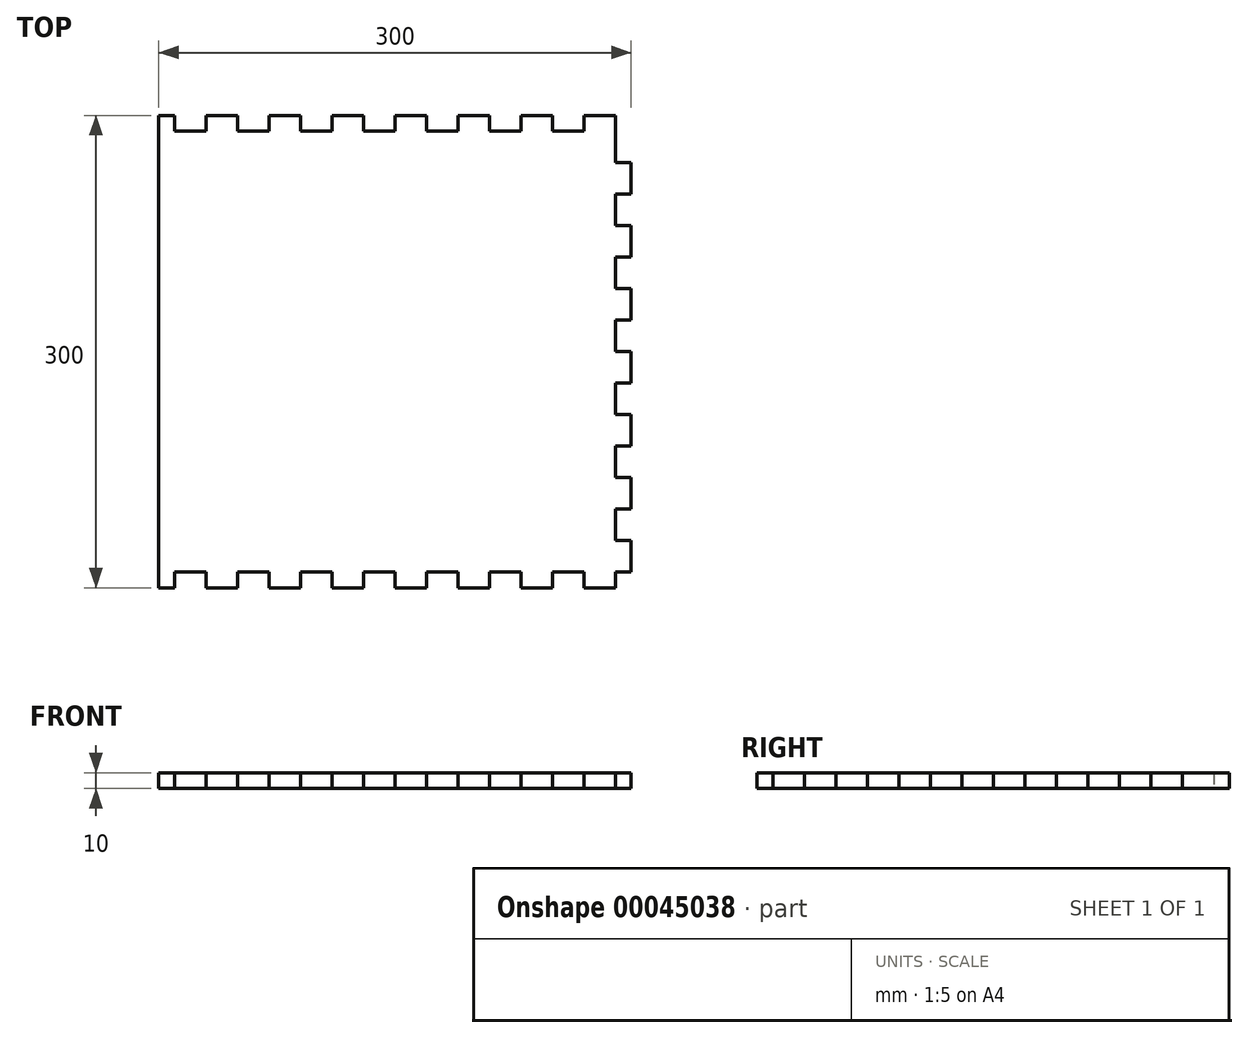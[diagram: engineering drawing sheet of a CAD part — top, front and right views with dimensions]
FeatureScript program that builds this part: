
annotation { "Feature Type Name" : "Feature", "Feature Type Description" : "" }
export const myFeature = defineFeature(function(context is Context, id is Id, definition is map)
    precondition{}
    {
        {
            var Q0;
            Q0=qCreatedBy(makeId("Top.planeOp"),FACE);
            var sketch = newSketch(context, id + "F0", { "sketchPlane" : qUnion([Q0])});
            skLineSegment(sketch, "E0.bottom", {"start": v(0, 0) * mm, "end": v(300, 0) * mm});
            skLineSegment(sketch, "E0.top", {"start": v(0, 300) * mm, "end": v(300, 300) * mm});
            skLineSegment(sketch, "E0.left", {"start": v(0, 0) * mm, "end": v(0, 300) * mm});
            skLineSegment(sketch, "E0.right", {"start": v(300, 0) * mm, "end": v(300, 300) * mm});
            skSolve(sketch);
        }
        {
            var Q0;
            Q0 = qSketchRegion(id + "F0", true);
            extrude(context, id + "F1", {"entities" : qUnion([Q0]), "depth" : 10 * mm});
        }
        {
            var Q0;
            Q0=makeQuery(id+"F0.imprint","IMPRINT",FACE,{"disambiguationData":[TD([[makeQuery(id+"F0.imprint","IMPRINT",EDGE,{"derivedFrom":sQuery(id+"F0.wireOp",EDGE,"E0.bottom")}),1.0]])]});
            var sketch = newSketch(context, id + "F2", { "sketchPlane" : qUnion([Q0])});
            skLineSegment(sketch, "E1.bottom", {"start": v(10, 0) * mm, "end": v(29.92, 0) * mm});
            skLineSegment(sketch, "E1.top", {"start": v(10, 10) * mm, "end": v(29.93, 10) * mm});
            skLineSegment(sketch, "E1.left", {"start": v(10, 0) * mm, "end": v(10, 10) * mm});
            skLineSegment(sketch, "E1.right", {"start": v(29.93, 0) * mm, "end": v(29.93, 10) * mm});
            skLineSegment(sketch, "E2.1.0.0", {"start": v(50, 0) * mm, "end": v(50, 10) * mm});
            skLineSegment(sketch, "E2.1.0.1", {"start": v(50, 0) * mm, "end": v(69.92, 0) * mm});
            skLineSegment(sketch, "E2.1.0.2", {"start": v(69.92, 0) * mm, "end": v(69.92, 10) * mm});
            skLineSegment(sketch, "E2.1.0.3", {"start": v(50, 10) * mm, "end": v(69.92, 10) * mm});
            skLineSegment(sketch, "E2.2.0.0", {"start": v(90, 0) * mm, "end": v(90, 10) * mm});
            skLineSegment(sketch, "E2.2.0.1", {"start": v(90, 0) * mm, "end": v(109.92, 0) * mm});
            skLineSegment(sketch, "E2.2.0.2", {"start": v(109.93, 0) * mm, "end": v(109.93, 10) * mm});
            skLineSegment(sketch, "E2.2.0.3", {"start": v(90, 10) * mm, "end": v(109.93, 10) * mm});
            skLineSegment(sketch, "E2.3.0.0", {"start": v(130, 0) * mm, "end": v(130, 10) * mm});
            skLineSegment(sketch, "E2.3.0.1", {"start": v(130, 0) * mm, "end": v(149.93, 0) * mm});
            skLineSegment(sketch, "E2.3.0.2", {"start": v(149.93, 0) * mm, "end": v(149.93, 10) * mm});
            skLineSegment(sketch, "E2.3.0.3", {"start": v(130, 10) * mm, "end": v(149.93, 10) * mm});
            skLineSegment(sketch, "E2.4.0.0", {"start": v(170, 0) * mm, "end": v(170, 10) * mm});
            skLineSegment(sketch, "E2.4.0.1", {"start": v(170, 0) * mm, "end": v(189.92, 0) * mm});
            skLineSegment(sketch, "E2.4.0.2", {"start": v(189.93, 0) * mm, "end": v(189.93, 10) * mm});
            skLineSegment(sketch, "E2.4.0.3", {"start": v(170, 10) * mm, "end": v(189.92, 10) * mm});
            skLineSegment(sketch, "E2.5.0.0", {"start": v(210, 0) * mm, "end": v(210, 10) * mm});
            skLineSegment(sketch, "E2.5.0.1", {"start": v(210, 0) * mm, "end": v(229.93, 0) * mm});
            skLineSegment(sketch, "E2.5.0.2", {"start": v(229.93, 0) * mm, "end": v(229.93, 10) * mm});
            skLineSegment(sketch, "E2.5.0.3", {"start": v(210, 10) * mm, "end": v(229.93, 10) * mm});
            skLineSegment(sketch, "E2.6.0.0", {"start": v(250, 0) * mm, "end": v(250, 10) * mm});
            skLineSegment(sketch, "E2.6.0.1", {"start": v(250, 0) * mm, "end": v(269.93, 0) * mm});
            skLineSegment(sketch, "E2.6.0.2", {"start": v(269.92, 0) * mm, "end": v(269.92, 10) * mm});
            skLineSegment(sketch, "E2.6.0.3", {"start": v(250, 10) * mm, "end": v(269.93, 10) * mm});
            skLineSegment(sketch, "E2.direction1", {"start": v(10, 0) * mm, "end": v(50, 0) * mm, "construction": true});
            skLineSegment(sketch, "E3.0.7.0", {"start": v(290, 0) * mm, "end": v(290, 10) * mm});
            skLineSegment(sketch, "E3.3.7.0", {"start": v(290, 0) * mm, "end": v(309.93, 0) * mm});
            skLineSegment(sketch, "E3.6.7.0", {"start": v(309.93, 0) * mm, "end": v(309.93, 10) * mm});
            skLineSegment(sketch, "E3.9.7.0", {"start": v(290, 10) * mm, "end": v(309.93, 10) * mm});
            skLineSegment(sketch, "E4.bottom", {"start": v(290, 30.07) * mm, "end": v(300, 30.07) * mm});
            skLineSegment(sketch, "E4.top", {"start": v(290, 50) * mm, "end": v(300, 50) * mm});
            skLineSegment(sketch, "E4.left", {"start": v(290, 30.07) * mm, "end": v(290, 50) * mm});
            skLineSegment(sketch, "E4.right", {"start": v(300, 30.07) * mm, "end": v(300, 50) * mm});
            skLineSegment(sketch, "E5.0.1.0", {"start": v(290, 70.08) * mm, "end": v(290, 90) * mm});
            skLineSegment(sketch, "E5.0.1.1", {"start": v(300, 70.08) * mm, "end": v(300, 90) * mm});
            skLineSegment(sketch, "E5.0.1.2", {"start": v(290, 70.08) * mm, "end": v(300, 70.08) * mm});
            skLineSegment(sketch, "E5.0.1.3", {"start": v(290, 90) * mm, "end": v(300, 90) * mm});
            skLineSegment(sketch, "E5.0.2.0", {"start": v(290, 110.08) * mm, "end": v(290, 130) * mm});
            skLineSegment(sketch, "E5.0.2.1", {"start": v(300, 110.08) * mm, "end": v(300, 130) * mm});
            skLineSegment(sketch, "E5.0.2.2", {"start": v(290, 110.08) * mm, "end": v(300, 110.08) * mm});
            skLineSegment(sketch, "E5.0.2.3", {"start": v(290, 130) * mm, "end": v(300, 130) * mm});
            skLineSegment(sketch, "E5.0.3.0", {"start": v(290, 150.07) * mm, "end": v(290, 170) * mm});
            skLineSegment(sketch, "E5.0.3.1", {"start": v(300, 150.07) * mm, "end": v(300, 170) * mm});
            skLineSegment(sketch, "E5.0.3.2", {"start": v(290, 150.07) * mm, "end": v(300, 150.07) * mm});
            skLineSegment(sketch, "E5.0.3.3", {"start": v(290, 170) * mm, "end": v(300, 170) * mm});
            skLineSegment(sketch, "E5.0.4.0", {"start": v(290, 190.07) * mm, "end": v(290, 210) * mm});
            skLineSegment(sketch, "E5.0.4.1", {"start": v(300, 190.07) * mm, "end": v(300, 210) * mm});
            skLineSegment(sketch, "E5.0.4.2", {"start": v(290, 190.07) * mm, "end": v(300, 190.07) * mm});
            skLineSegment(sketch, "E5.0.4.3", {"start": v(290, 210) * mm, "end": v(300, 210) * mm});
            skLineSegment(sketch, "E5.0.5.0", {"start": v(290, 230.07) * mm, "end": v(290, 250) * mm});
            skLineSegment(sketch, "E5.0.5.1", {"start": v(300, 230.07) * mm, "end": v(300, 250) * mm});
            skLineSegment(sketch, "E5.0.5.2", {"start": v(290, 230.07) * mm, "end": v(300, 230.07) * mm});
            skLineSegment(sketch, "E5.0.5.3", {"start": v(290, 250) * mm, "end": v(300, 250) * mm});
            skLineSegment(sketch, "E5.0.6.0", {"start": v(290, 270.07) * mm, "end": v(290, 290) * mm});
            skLineSegment(sketch, "E5.0.6.1", {"start": v(300, 270.07) * mm, "end": v(300, 290) * mm});
            skLineSegment(sketch, "E5.0.6.2", {"start": v(290, 270.07) * mm, "end": v(300, 270.07) * mm});
            skLineSegment(sketch, "E5.0.6.3", {"start": v(290, 290) * mm, "end": v(300, 290) * mm});
            skLineSegment(sketch, "E5.direction1", {"start": v(290, 30.07) * mm, "end": v(315, 30.07) * mm, "construction": true});
            skLineSegment(sketch, "E5.direction2", {"start": v(290, 30.07) * mm, "end": v(290, 70.08) * mm, "construction": true});
            skLineSegment(sketch, "E6.top", {"start": v(290, 300) * mm, "end": v(300, 300) * mm});
            skLineSegment(sketch, "E6.left", {"start": v(290, 290) * mm, "end": v(290, 300) * mm});
            skLineSegment(sketch, "E6.right", {"start": v(300, 290) * mm, "end": v(300, 300) * mm});
            skLineSegment(sketch, "E7.bottom", {"start": v(269.92, 290) * mm, "end": v(250, 290) * mm});
            skLineSegment(sketch, "E7.top", {"start": v(269.92, 300) * mm, "end": v(250, 300) * mm});
            skLineSegment(sketch, "E7.left", {"start": v(269.92, 290) * mm, "end": v(269.92, 300) * mm});
            skLineSegment(sketch, "E7.right", {"start": v(250, 290) * mm, "end": v(250, 300) * mm});
            skLineSegment(sketch, "E8.1.0.0", {"start": v(229.92, 290) * mm, "end": v(210, 290) * mm});
            skLineSegment(sketch, "E8.1.0.1", {"start": v(210, 290) * mm, "end": v(210, 300) * mm});
            skLineSegment(sketch, "E8.1.0.2", {"start": v(229.92, 290) * mm, "end": v(229.92, 300) * mm});
            skLineSegment(sketch, "E8.1.0.3", {"start": v(229.92, 300) * mm, "end": v(210, 300) * mm});
            skLineSegment(sketch, "E8.2.0.0", {"start": v(189.92, 290) * mm, "end": v(170, 290) * mm});
            skLineSegment(sketch, "E8.2.0.1", {"start": v(170, 290) * mm, "end": v(170, 300) * mm});
            skLineSegment(sketch, "E8.2.0.2", {"start": v(189.92, 290) * mm, "end": v(189.92, 300) * mm});
            skLineSegment(sketch, "E8.2.0.3", {"start": v(189.92, 300) * mm, "end": v(170, 300) * mm});
            skLineSegment(sketch, "E8.3.0.0", {"start": v(149.92, 290) * mm, "end": v(130, 290) * mm});
            skLineSegment(sketch, "E8.3.0.1", {"start": v(130, 290) * mm, "end": v(130, 300) * mm});
            skLineSegment(sketch, "E8.3.0.2", {"start": v(149.92, 290) * mm, "end": v(149.92, 300) * mm});
            skLineSegment(sketch, "E8.3.0.3", {"start": v(149.92, 300) * mm, "end": v(130, 300) * mm});
            skLineSegment(sketch, "E8.4.0.0", {"start": v(109.92, 290) * mm, "end": v(90, 290) * mm});
            skLineSegment(sketch, "E8.4.0.1", {"start": v(90, 290) * mm, "end": v(90, 300) * mm});
            skLineSegment(sketch, "E8.4.0.2", {"start": v(109.92, 290) * mm, "end": v(109.92, 300) * mm});
            skLineSegment(sketch, "E8.4.0.3", {"start": v(109.92, 300) * mm, "end": v(90, 300) * mm});
            skLineSegment(sketch, "E8.5.0.0", {"start": v(69.92, 290) * mm, "end": v(50, 290) * mm});
            skLineSegment(sketch, "E8.5.0.1", {"start": v(50, 290) * mm, "end": v(50, 300) * mm});
            skLineSegment(sketch, "E8.5.0.2", {"start": v(69.92, 290) * mm, "end": v(69.92, 300) * mm});
            skLineSegment(sketch, "E8.5.0.3", {"start": v(69.92, 300) * mm, "end": v(50, 300) * mm});
            skLineSegment(sketch, "E8.6.0.0", {"start": v(29.92, 290) * mm, "end": v(10, 290) * mm});
            skLineSegment(sketch, "E8.6.0.1", {"start": v(10, 290) * mm, "end": v(10, 300) * mm});
            skLineSegment(sketch, "E8.6.0.2", {"start": v(29.92, 290) * mm, "end": v(29.92, 300) * mm});
            skLineSegment(sketch, "E8.6.0.3", {"start": v(29.92, 300) * mm, "end": v(10, 300) * mm});
            skLineSegment(sketch, "E8.direction1", {"start": v(250, 290) * mm, "end": v(210, 290) * mm, "construction": true});
            skSolve(sketch);
        }
        {
            var Q0;
            Q0 = qSketchRegion(id + "F2", true);
            var Q1;
            Q1 = qConstructionFilter(qBodyType(qCreatedBy(id + "F2" ,EDGE), BodyType.WIRE), ConstructionObject.NO);
            extrude(context, id + "F3", {"entities" : qUnion([Q0]), "operationType" : NewBodyOperationType.REMOVE, "surfaceEntities" : qUnion([Q1]), "endBound" : BoundingType.THROUGH_ALL, "depth" : 25 * mm});
        }
    });
